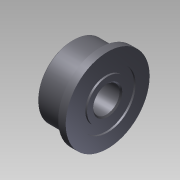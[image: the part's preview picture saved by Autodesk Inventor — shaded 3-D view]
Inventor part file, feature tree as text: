
AUTODESK INVENTOR PART (.ipt)
format: ipt  version: 2015 SP1 (Build 190203100, 203)  size: 157,696 bytes
history: native  units: in
note: dims shown in document units (in); Inventor stores cm internally (conversion verified against a paired STEP export)
features: chamfer x1, other x1, imported_body x1
ambient origin geometry x8: Origin, YZ Plane, XZ Plane, XY Plane, X Axis, Y Axis, Z Axis, Center Point
bodies: Body1 (feature_tree)
feature tree (3):
  chamfer  "Chamfer1"  [1 undecoded]
  other  "BB-031"
  imported_body  "Base1"
note: 1 required parameter value undecoded (feature->parameter linkage not recoverable at this tier; creation-order binding heuristic only, values carry confidence <= 0.55)
